# Revit family: Haworth_UniGroupToo_Panel_GlazedAddOn
name_source: partatom
category: Furniture Systems
revit_build: Autodesk Revit 2018 (Build: 20170223_1515(x64)
units: mm (PartAtom-declared; Revit-internal decimal feet)

## family parameters
Always vertical = Yes
Cut with Voids When Loaded = No
OmniClass Number = 23.40.70.14.64.21
OmniClass Title = Systems Furniture
Part Type = Normal
Room Calculation Point = No
Round Connector Dimension = Use Diameter
Shared = No
Work Plane-Based = No

## types (1)
- 24w 16h
    Actual Height = 16 1/2"
    Actual Width = 24"
    Assembly Code = E2020500
    Bottom Trim Width = 3/8"
    Custom Size = No
    Description = Haworth - UniGroup Too - Panel - Add-On - Glazed
    Glass Finish = Haworth _ Glass _ Frosted
    Glaze Inset = 3/4"
    Glazed Trim Sides = 1 3/8"
    Glazed Trim Top = 1 3/4"
    Height = 16 1/2"
    Manufacturer = Haworth
    Max. Height = 16 1/2"
    Max. Width = 60"
    Min. Height = 16 1/2"
    Min. Width = 24"
    Model = Haworth - UniGroup Too - Panel - Add-On - Glazed
    Panel Depth = 1/2"
    Raceway Panel Width = 24"
    Rail Height = 16"
    Revision Number = 2
    Size = Verify Final Dim. w/ Haworth
    Standard Heights = 16 inches
    Standard Widths = 24, 30, 36, 42, 48, 60 inches
    Sustainability Info = http://www.haworth.com
    Top Trim Height = 1/2"
    Trim Depth = 2"
    Trim Finish = Haworth _ Metal _ Brushed Aluminum
    Trim Inset = 1/8"
    URL = www.haworth.com
    URL - Product = http://www.haworth.com
    Warranty = http://www.haworth.com
    Width = 24"

## geometry (parser evidence)
native form markers: Sweep x6
no freeform markers — native parametric forms only
